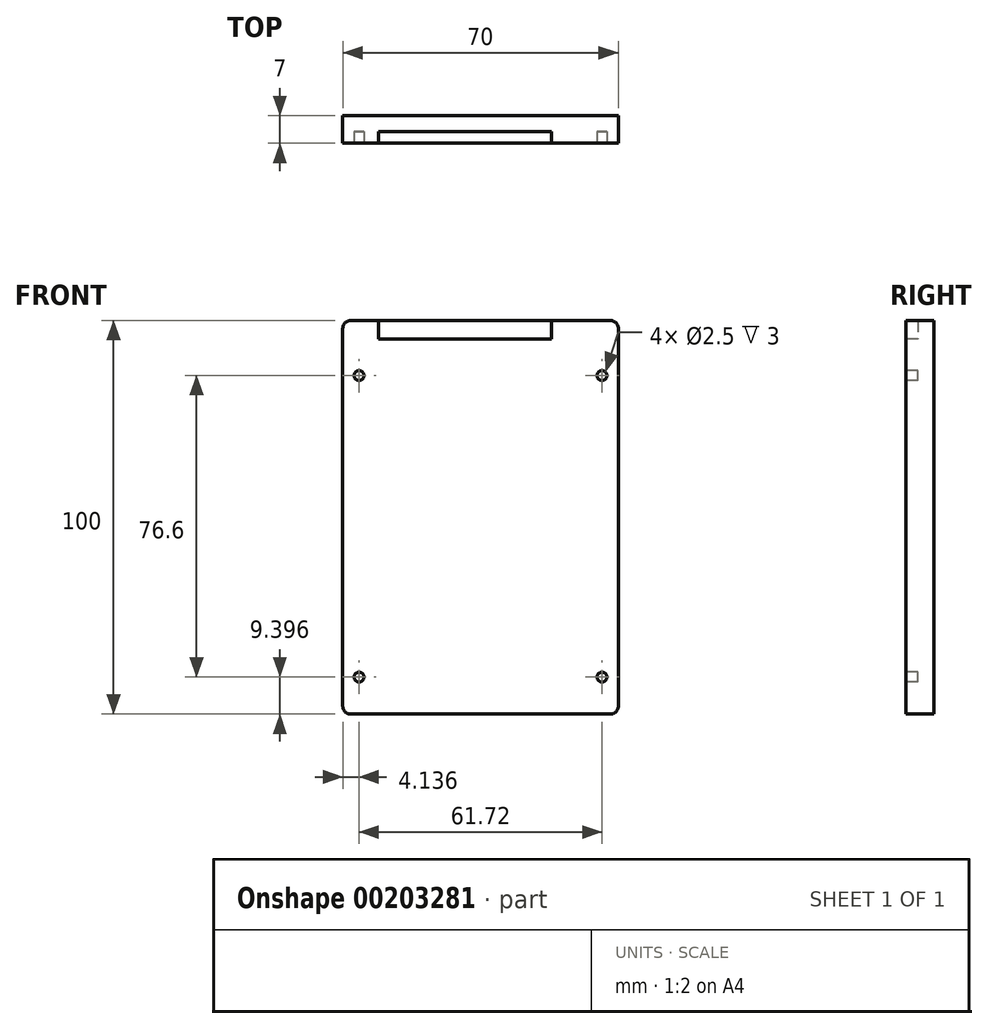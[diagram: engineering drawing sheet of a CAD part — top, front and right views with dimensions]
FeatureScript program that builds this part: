
annotation { "Feature Type Name" : "Feature", "Feature Type Description" : "" }
export const myFeature = defineFeature(function(context is Context, id is Id, definition is map)
    precondition{}
    {
        {
            var Q0;
            Q0=qCreatedBy(makeId("Front.planeOp"),FACE);
            var sketch = newSketch(context, id + "F0", { "sketchPlane" : qUnion([Q0])});
            skLineSegment(sketch, "E0.bottom", {"start": v(8.89, 110) * mm, "end": v(78.89, 110) * mm});
            skLineSegment(sketch, "E0.top", {"start": v(8.89, 10) * mm, "end": v(78.89, 10) * mm});
            skLineSegment(sketch, "E0.left", {"start": v(8.89, 110) * mm, "end": v(8.89, 10) * mm});
            skLineSegment(sketch, "E0.right", {"start": v(78.89, 110) * mm, "end": v(78.89, 10) * mm});
            skSolve(sketch);
        }
        {
            var Q0;
            Q0=makeQuery(id+"F0.imprint","IMPRINT",FACE,{"disambiguationData":[TD([[makeQuery(id+"F0.imprint","IMPRINT",EDGE,{"derivedFrom":sQuery(id+"F0.wireOp",EDGE,"E0.bottom")}),-1.0]])]});
            extrude(context, id + "F1", {"entities" : qUnion([Q0]), "depth" : 7 * mm});
        }
        {
            var Q0;
            Q0=makeQuery(id+"F1.opExtrude","SWEPT_EDGE",EDGE,{"disambiguationData":[OSD([sQuery(id+"F0.wireOp",EDGE,"E0.bottom"),sQuery(id+"F0.wireOp",EDGE,"E0.left")])]});
            var Q1;
            Q1=makeQuery(id+"F1.opExtrude","SWEPT_EDGE",EDGE,{"disambiguationData":[OSD([sQuery(id+"F0.wireOp",EDGE,"E0.top"),sQuery(id+"F0.wireOp",EDGE,"E0.left")])]});
            var Q2;
            Q2=makeQuery(id+"F1.opExtrude","SWEPT_EDGE",EDGE,{"disambiguationData":[OSD([sQuery(id+"F0.wireOp",EDGE,"E0.top"),sQuery(id+"F0.wireOp",EDGE,"E0.right")])]});
            var Q3;
            Q3=makeQuery(id+"F1.opExtrude","SWEPT_EDGE",EDGE,{"disambiguationData":[OSD([sQuery(id+"F0.wireOp",EDGE,"E0.bottom"),sQuery(id+"F0.wireOp",EDGE,"E0.right")])]});
            fillet(context, id + "F2", {"entities" : qUnion([Q0, Q1, Q2, Q3]), "radius" : 2 * mm, "tangentPropagation" : true, "allowEdgeOverflow" : false});
        }
        {
            var Q0;
            Q0=makeQuery(id+"F1.opExtrude","CAP_FACE",FACE,{"disambiguationData":[OSD([sQuery(id+"F0.wireOp",EDGE,"E0.bottom"),sQuery(id+"F0.wireOp",EDGE,"E0.top"),sQuery(id+"F0.wireOp",EDGE,"E0.left"),sQuery(id+"F0.wireOp",EDGE,"E0.right")])],"isStart":false});
            var sketch = newSketch(context, id + "F3", { "sketchPlane" : qUnion([Q0])});
            skLineSegment(sketch, "E1", {"start": v(13.03, 96) * mm, "end": v(74.75, 96) * mm, "construction": true});
            skLineSegment(sketch, "E2", {"start": v(43.89, 96) * mm, "end": v(43.89, 110) * mm, "construction": true});
            skCircle(sketch, "E3", {"center": v(13.03, 96) * mm, "radius": 1.25 * mm});
            skCircle(sketch, "E4", {"center": v(74.75, 96) * mm, "radius": 1.25 * mm});
            skLineSegment(sketch, "E5", {"start": v(13.03, 19.4) * mm, "end": v(74.75, 19.4) * mm, "construction": true});
            skLineSegment(sketch, "E6", {"start": v(43.89, 96) * mm, "end": v(43.89, 19.4) * mm, "construction": true});
            skCircle(sketch, "E7", {"center": v(13.03, 19.4) * mm, "radius": 1.25 * mm});
            skCircle(sketch, "E8", {"center": v(74.75, 19.4) * mm, "radius": 1.25 * mm});
            skLineSegment(sketch, "E9.bottom", {"start": v(17.94, 110) * mm, "end": v(61.95, 110) * mm});
            skLineSegment(sketch, "E9.top", {"start": v(17.94, 105.3) * mm, "end": v(61.95, 105.3) * mm});
            skLineSegment(sketch, "E9.left", {"start": v(17.94, 110) * mm, "end": v(17.94, 105.3) * mm});
            skLineSegment(sketch, "E9.right", {"start": v(61.95, 110) * mm, "end": v(61.95, 105.3) * mm});
            skSolve(sketch);
        }
        {
            var Q0;
            Q0 = qSketchRegion(id + "F3", true);
            extrude(context, id + "F4", {"entities" : qUnion([Q0]), "operationType" : NewBodyOperationType.REMOVE, "oppositeDirection" : true, "depth" : 3 * mm});
        }
    });
